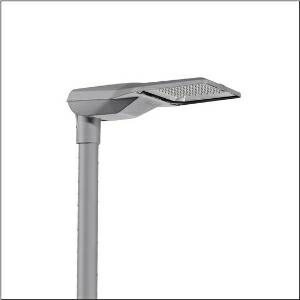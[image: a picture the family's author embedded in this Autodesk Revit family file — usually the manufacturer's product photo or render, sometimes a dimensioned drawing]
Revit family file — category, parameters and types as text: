
# Revit family: streetlight_sl_21_iq_midi___stw1_0a_5xe3e41g08mb_cdbd
name_source: partatom
category: Lighting Fixtures
units: mm (PartAtom-declared; Revit-internal decimal feet)

## family parameters
Cut with Voids When Loaded = No
Host = Face
Light Source = No
Part Type = Normal
Room Calculation Point = No
Round Connector Dimension = Use Diameter
Shared = No

## types (1)
- --- (1 x LED, 20360 lm, 146.7 W, 4000K)
    Apparent Load = 147 VA
    CIE Flux Codes = 38 75 98 100 100
    Color Rendering = 70
    Color Temperature = 4000K
    Default Elevation = 1800 mm
    Description = Streetlight SL 21 iQ midi, mast luminaire, primary light control with lens, of PMMA, primary optical cover: cover, of toughened safety glass, transparent, light distribution: STW1.0a, light emission: direct distribution, primary light characteristic: asymmetric, installation type: post-top, side-entry, LED, High Power LED, rated luminous flux: 20.360lm, luminous efficacy: 139lm/W, light colour: 740, colour temperature: 4000K, control gear: iQ Street-Remote, control: Street-Remote, Auto-Match, Temp-Guard, Lumen-Switch, Night-Set, Smart-Wire, Light-Fading, Desk-Remote (wireless, voltage-free reading and setting of iQ features in the workshop via application-optimized NFC function/RFID function), optimised constant luminous flux control (CLO 2.0), pre-setting: linear dimming characteristic, mains connection: 230..240V, AC, 50/60Hz, start of lifetime: 147W, end of service life: 161W, reduction: 62W, luminaire housing, of diecast aluminium, powder-coated, SITECO metallic grey (DB 702S), corrosivity category C5 high according to DIN EN ISO 12944, please order mast flange separately, inclination adjustable: 0°, 5°, 10°, 15°, sealing non-destructively replaceable, multi-level sealing system, length: 644mm, width: 335mm, height: 110mm, mast flange for spigot size: 42mm (side-entry): 5XC10008XM4, 60/48mm (side-entry/post-top): 5XC10108XM2, 76/60mm (side-entry/post-top): 5XC10108XM1, mounting height: 4..8m, protection rating (complete): IP66, insulation class (complete): insulation class II (safety insulation), certification: CE, ENEC, ENEC+, VDE, impact resistance: IK10, permissible operating ambient temperature for outdoor applications: -40..+50°C, standard-compliant lighting for roads and squares, packaging unit: 1 piece

Light Distribution: STW1.0a
    Height = 111 mm
    Lamp = 1 x LED
    Lamp Light Flux = 20360 lm
    Lamp Power = 146.7 W
    Lamp count = 1
    Length = 644 mm
    Luminous efficacy = 139 lm/W
    Manufacturer = Siteco
    ModVariant = No
    Model = 5XE3E41G08MB
    Number of Poles = 1
    OnlyDefault = Yes
    Power Factor = 1
    Product Name = Streetlight SL 21 iQ midi | STW1.0a
    Product group = mast luminaire | pylon top
    ProductGroupID = 6100
    Protection Class = Protection class II
    Protection Degree = IP 66
    RLX_Detail_Level = 1
    RLX_Emergency_Light_Flux = 0 lm
    RLX_Emergency_Type = 0
    RLX_Emergency_Type_DB = No
    RlxData = <blob elided: 26997 chars, md5=eb29b7a0>
    Socket = socket
    Standby Power = 0 W
    System Light Flux = 20360 lm
    System Power = 147 W
    Type Comments = factory setting: luminous flux: 100 % | dim-lin: 254 | 753 mA
    Type Image = l_1004298.jpg
    URL = http://relux.com
    VarID = @adj_185487
    Voltage = 0 V
    Weight = 0.00 kg
    Width = 336 mm

## geometry (parser evidence)
native form markers: Blend x4, Sweep x12
no freeform markers — native parametric forms only
